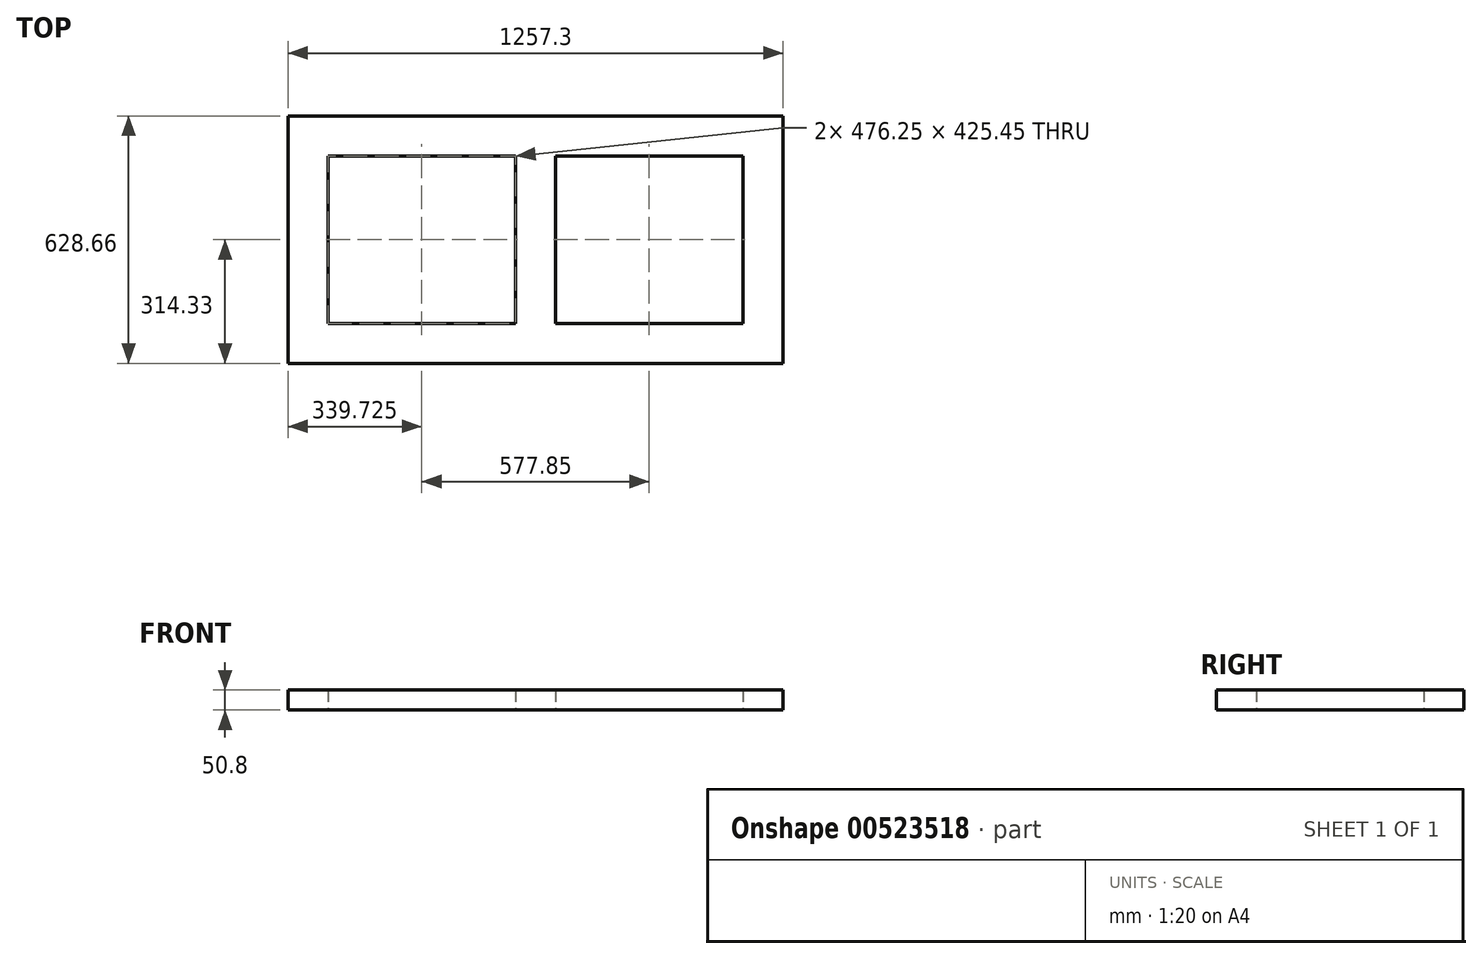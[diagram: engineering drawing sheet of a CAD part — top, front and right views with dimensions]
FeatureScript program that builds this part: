
annotation { "Feature Type Name" : "Feature", "Feature Type Description" : "" }
export const myFeature = defineFeature(function(context is Context, id is Id, definition is map)
    precondition{}
    {
        {
            var Q0;
            Q0=qCreatedBy(makeId("Top.planeOp"),FACE);
            var sketch = newSketch(context, id + "F0", { "sketchPlane" : qUnion([Q0])});
            skLineSegment(sketch, "E0.bottom", {"start": v(-628.65, 314.33) * mm, "end": v(628.65, 314.33) * mm});
            skLineSegment(sketch, "E0.top", {"start": v(-628.65, -314.33) * mm, "end": v(628.65, -314.33) * mm});
            skLineSegment(sketch, "E0.left", {"start": v(-628.65, 314.33) * mm, "end": v(-628.65, -314.33) * mm});
            skLineSegment(sketch, "E0.right", {"start": v(628.65, 314.33) * mm, "end": v(628.65, -314.33) * mm});
            skPoint(sketch, "E0.middle", {"position": v(0, 0) * mm});
            skLineSegment(sketch, "E1", {"start": v(-628.65, 0) * mm, "end": v(-527.05, 0) * mm, "construction": true});
            skPoint(sketch, "E1.endSnap0", {"position": v(-628.65, 0) * mm});
            skLineSegment(sketch, "E2", {"start": v(628.65, 0) * mm, "end": v(527.05, 0) * mm, "construction": true});
            skPoint(sketch, "E2.endSnap0", {"position": v(628.65, 0) * mm});
            skLineSegment(sketch, "E3", {"start": v(0, 0) * mm, "end": v(-50.8, 0) * mm, "construction": true});
            skLineSegment(sketch, "E4", {"start": v(0, 0) * mm, "end": v(50.8, 0) * mm, "construction": true});
            skLineSegment(sketch, "E5.bottom", {"start": v(-527.05, 212.73) * mm, "end": v(-50.8, 212.73) * mm});
            skLineSegment(sketch, "E5.top", {"start": v(-527.05, -212.73) * mm, "end": v(-50.8, -212.73) * mm});
            skLineSegment(sketch, "E5.left", {"start": v(-527.05, 212.73) * mm, "end": v(-527.05, -212.73) * mm});
            skLineSegment(sketch, "E5.right", {"start": v(-50.8, 212.73) * mm, "end": v(-50.8, -212.73) * mm});
            skLineSegment(sketch, "E6.bottom", {"start": v(50.8, 212.73) * mm, "end": v(527.05, 212.73) * mm});
            skLineSegment(sketch, "E6.top", {"start": v(50.8, -212.73) * mm, "end": v(527.05, -212.73) * mm});
            skLineSegment(sketch, "E6.left", {"start": v(50.8, 212.73) * mm, "end": v(50.8, -212.73) * mm});
            skLineSegment(sketch, "E6.right", {"start": v(527.05, 212.73) * mm, "end": v(527.05, -212.73) * mm});
            skSolve(sketch);
        }
        {
            var Q0;
            Q0=makeQuery(id+"F0.imprint","IMPRINT",FACE,{"disambiguationData":[TD([[makeQuery(id+"F0.imprint","IMPRINT",EDGE,{"derivedFrom":sQuery(id+"F0.wireOp",EDGE,"E0.bottom")}),-1.0]])]});
            extrude(context, id + "F1", {"entities" : qUnion([Q0]), "endBound" : BoundingType.SYMMETRIC, "depth" : 50.8 * mm, "offsetDistance" : 25.4 * mm});
        }
    });
